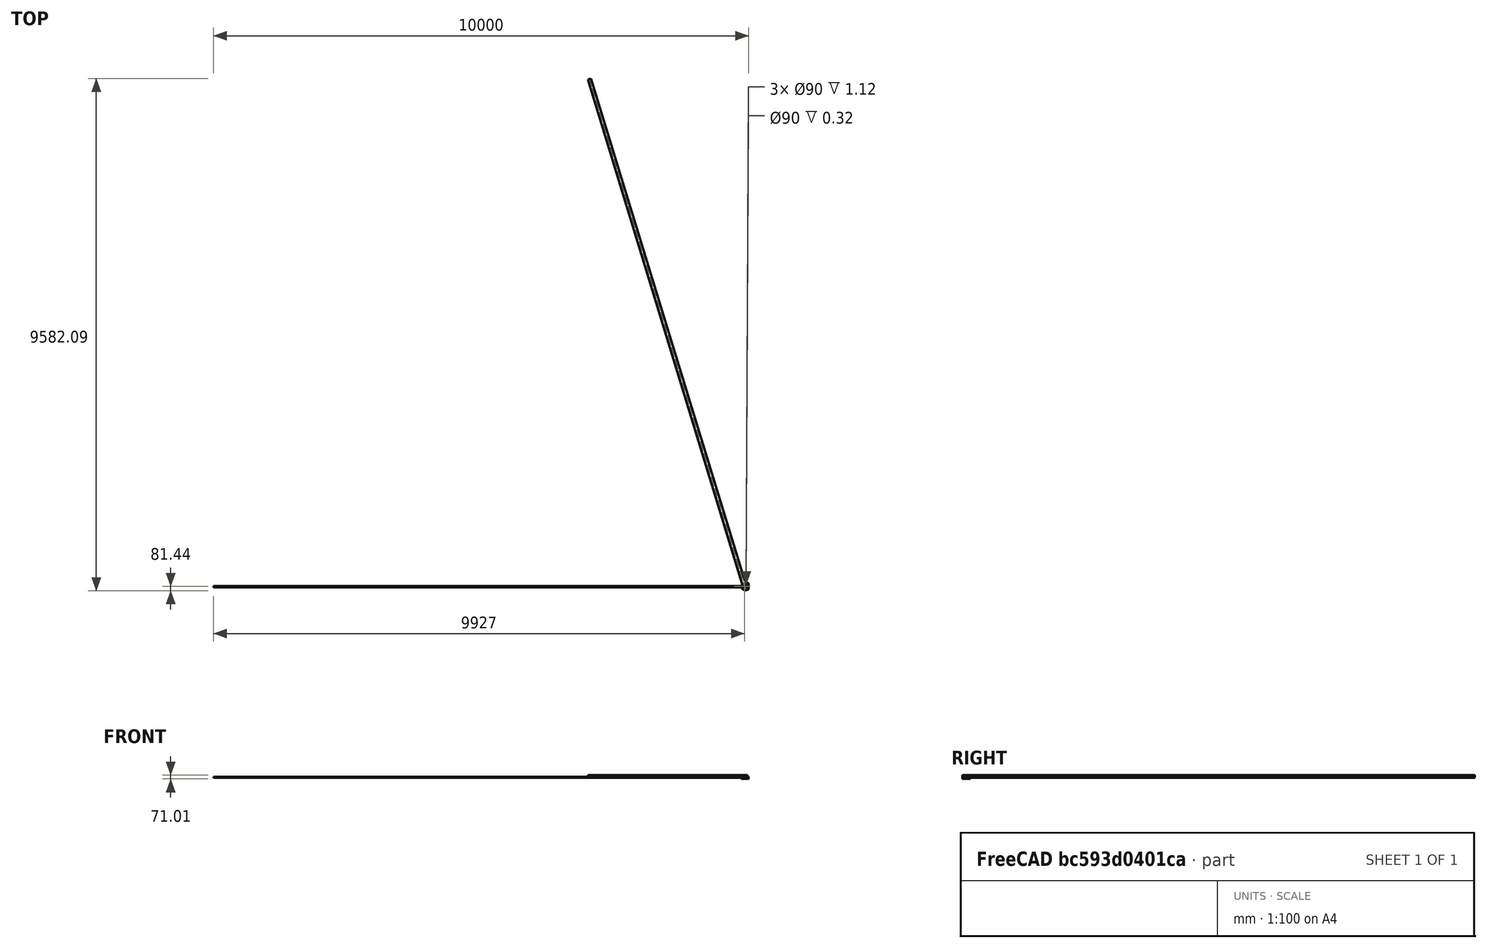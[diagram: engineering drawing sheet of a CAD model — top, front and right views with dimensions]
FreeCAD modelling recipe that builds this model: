
FCSTD DOCUMENT  (FreeCAD 0.16R)
Label: chainguard25TRev1.V2
License: All rights reserved
LicenseURL: http://en.wikipedia.org/wiki/All_rights_reserved
objects: Sketcher::SketchObject×14, PartDesign::Pocket×8, PartDesign::Pad×5, PartDesign::Fillet×5, Part::FeaturePython×3, Mesh::Feature×3
note: 48 computed .brp shape members not serialized (recipe doc carries the construction recipe); baked Part::Feature solids carry a one-line shape summary decoded from their .brp

FEATURE [Sketcher::SketchObject] Sketch001
  sketch-geometry (7):
    g0: LineSegment StartX=60 StartY=64 StartZ=0 EndX=0 EndY=64 EndZ=0
    g1: LineSegment StartX=60 StartY=-64 StartZ=0 EndX=0 EndY=-64 EndZ=0
    g2: ArcOfCircle CenterX=8.21903e-05 CenterY=0 CenterZ=0 NormalX=0 NormalY=0 NormalZ=1 Radius=64 StartAngle=1.5708 EndAngle=4.71239
    g3: Circle CenterX=0 CenterY=0 CenterZ=0 NormalX=0 NormalY=0 NormalZ=1 Radius=45
    g4: ArcOfCircle CenterX=60 CenterY=51 CenterZ=0 NormalX=0 NormalY=0 NormalZ=1 Radius=13 StartAngle=0 EndAngle=1.5708
    g5: ArcOfCircle CenterX=60 CenterY=-51 CenterZ=0 NormalX=0 NormalY=0 NormalZ=1 Radius=13 StartAngle=4.71239 EndAngle=6.28319
    g6: LineSegment StartX=73 StartY=51 StartZ=0 EndX=73 EndY=-51 EndZ=0
  constraints (23):
    c: Horizontal(g0)
    c: Horizontal(g1)
    c: Coincident(g2,g1)
    c: Coincident(g0,g2)
    c: DistanceX(g1,g0) = 0
    c: Equal(g0,g1)
    c: DistanceY(g1,g0) = 128
    c: Radius(g2) = 64
    c: Symmetric(g1,g0,g-1)
    c: Radius(g3) = 45
    c: Coincident(g3,g-1)
    c: PointOnObject(g4,g0)
    c: Radius(g4) = 13
    c: DistanceX(g0,g0) = 60
    c: Equal(g5,g4)
    c: Vertical(g6)
    c: DistanceX(g-1,g6) = 73
    c: Symmetric(g6,g6,g-1)
    c: DistanceY(g6,g6) = 102
    c: Coincident(g4,g6)
    c: Coincident(g5,g6)
    c: Coincident(g1,g5)
    c: Coincident(g0,g4)
FEATURE [PartDesign::Pad] Pad  label="Faceplate"
  Length = 1.12
  Length2 = 100
  Reversed = true
  Sketch = -> Sketch001
  Type = 0
FEATURE [Sketcher::SketchObject] Sketch002
  sketch-geometry (8):
    g0: LineSegment StartX=60 StartY=64 StartZ=0 EndX=0 EndY=64 EndZ=0
    g1: LineSegment StartX=60 StartY=-64 StartZ=0 EndX=0 EndY=-64 EndZ=0
    g2: ArcOfCircle CenterX=6.44712e-05 CenterY=0 CenterZ=0 NormalX=0 NormalY=0 NormalZ=1 Radius=64 StartAngle=1.5708 EndAngle=4.71239
    g3: LineSegment StartX=0 StartY=62 StartZ=0 EndX=60 EndY=62 EndZ=0
    g4: LineSegment StartX=0 StartY=-62 StartZ=0 EndX=60 EndY=-62 EndZ=0
    g5: LineSegment StartX=60 StartY=64 StartZ=0 EndX=60 EndY=62 EndZ=0
    g6: LineSegment StartX=60 StartY=-62 StartZ=0 EndX=60 EndY=-64 EndZ=0
    g7: ArcOfCircle CenterX=1.45954e-05 CenterY=0 CenterZ=0 NormalX=0 NormalY=0 NormalZ=1 Radius=62 StartAngle=1.5708 EndAngle=4.71239
  constraints (25):
    c: Horizontal(g0)
    c: Horizontal(g1)
    c: Coincident(g2,g1)
    c: Coincident(g0,g2)
    c: DistanceX(g1,g0) = 0
    c: Equal(g0,g1)
    c: DistanceY(g1,g0) = 128
    c: Radius(g2) = 64
    c: Symmetric(g1,g0,g-1)
    c: Radius(g7) = 62
    c: Parallel(g0,g3)
    c: DistanceY(g3,g0) = 2
    c: DistanceY(g1,g4) = 2
    c: Parallel(g4,g1)
    c: DistanceX(g0,g3) = 0
    c: DistanceX(g4) = 0
    c: DistanceX(g0) = 60
    c: Equal(g3,g0)
    c: Equal(g4,g0)
    c: Coincident(g4,g6)
    c: Coincident(g6,g1)
    c: Coincident(g5,g3)
    c: Coincident(g5,g0)
    c: Coincident(g7,g3)
    c: Coincident(g7,g4)
FEATURE [PartDesign::Pad] Pad001  label="Connector"
  Length = 8
  Length2 = 100
  Sketch = -> Sketch002
  Type = 0
FEATURE [Sketcher::SketchObject] Sketch004  label="BossST"
  sketch-geometry (4):
    g0: LineSegment StartX=42 StartY=-62 StartZ=0 EndX=2 EndY=-62 EndZ=0
    g1: LineSegment StartX=2 StartY=-62 StartZ=0 EndX=2 EndY=-78.2292 EndZ=0
    g2: LineSegment StartX=42 StartY=-66 StartZ=0 EndX=42 EndY=-62 EndZ=0
    g3: LineSegment StartX=2 StartY=-78.2292 StartZ=0 EndX=42 EndY=-66 EndZ=0
  constraints (12):
    c: Coincident(g0,g1)
    c: Vertical(g1)
    c: Vertical(g2)
    c: DistanceX(g0,g0) = 40
    c: DistanceX(g-1,g1) = 2
    c: Angle(g3) = 0.296706
    c: DistanceY(g0,g-1) = 62
    c: Horizontal(g0)
    c: DistanceY(g2,g2) = 4
    c: Coincident(g2,g0)
    c: Coincident(g3,g2)
    c: Coincident(g1,g3)
FEATURE [Sketcher::SketchObject] Sketch007
  Placement = pos=(0,0,45) rot=(0,0,1;0rad)
  sketch-geometry (4):
    g0: LineSegment StartX=-4.66376 StartY=-53.9534 StartZ=0 EndX=-5.90948 EndY=-71.4651 EndZ=0
    g1: LineSegment StartX=-5.90948 StartY=-71.4651 StartZ=0 EndX=38.1328 EndY=-58 EndZ=0
    g2: LineSegment StartX=38.1328 StartY=-58 StartZ=0 EndX=37.116 EndY=-54.0061 EndZ=0
    g3: LineSegment StartX=37.116 StartY=-54.0061 StartZ=0 EndX=-4.66376 EndY=-53.9534 EndZ=0
  constraints (9):
    c: Coincident(g0,g1)
    c: Coincident(g1,g2)
    c: Coincident(g2,g3)
    c: Coincident(g0,g3)
    c: Distance(g3) = 41.7798
    c: Distance(g0) = 17.5559
    c: Distance(g1) = 46.0546
    c: Distance(g2) = 4.12132
    c: DistanceX(g0,g-1) = 4.66376
FEATURE [PartDesign::Pocket] Pocket002  label="STpocket1"
  Length = 30
  Sketch = -> Sketch007
  Type = 0
FEATURE [Sketcher::SketchObject] Sketch
  Support = -> Pad [Face8]
  sketch-geometry (4):
    g0: LineSegment StartX=65 StartY=35 StartZ=0 EndX=73 EndY=35 EndZ=0
    g1: LineSegment StartX=73 StartY=35 StartZ=0 EndX=73 EndY=-35 EndZ=0
    g2: LineSegment StartX=73 StartY=-35 StartZ=0 EndX=65 EndY=-35 EndZ=0
    g3: LineSegment StartX=65 StartY=-35 StartZ=0 EndX=65 EndY=35 EndZ=0
  constraints (12):
    c: Coincident(g0,g1)
    c: Coincident(g1,g2)
    c: Coincident(g2,g3)
    c: Coincident(g3,g0)
    c: Horizontal(g0)
    c: Horizontal(g2)
    c: Vertical(g1)
    c: Vertical(g3)
    c: Symmetric(g0,g2,g-1)
    c: DistanceX(g0,g0) = 8
    c: DistanceX(g-1,g0) = 73
    c: DistanceY(g3,g3) = 70
FEATURE [PartDesign::Pad] Pad003  label="SyncStiffener"
  Length = 3
  Length2 = 100
  Sketch = -> Sketch
  Type = 0
FEATURE [Sketcher::SketchObject] Sketch008
  Placement = pos=(0,0,3) rot=(0,0,1;0rad)
  Support = -> Pad003 [Face14]
  sketch-geometry (4):
    g0: LineSegment StartX=67 StartY=8 StartZ=0 EndX=73 EndY=8 EndZ=0
    g1: LineSegment StartX=73 StartY=8 StartZ=0 EndX=73 EndY=-22 EndZ=0
    g2: LineSegment StartX=73 StartY=-22 StartZ=0 EndX=67 EndY=-22 EndZ=0
    g3: LineSegment StartX=67 StartY=-22 StartZ=0 EndX=67 EndY=8 EndZ=0
  constraints (12):
    c: Coincident(g0,g1)
    c: Coincident(g1,g2)
    c: Coincident(g2,g3)
    c: Coincident(g3,g0)
    c: Horizontal(g0)
    c: Horizontal(g2)
    c: Vertical(g1)
    c: Vertical(g3)
    c: DistanceX(g0) = 73
    c: DistanceX(g0,g0) = 6
    c: DistanceY(g1,g1) = 30
    c: DistanceY(g-1,g0) = 8
FEATURE [PartDesign::Pad] Pad004  label="SyncTubeBoss"
  Length = 41
  Length2 = 100
  Sketch = -> Sketch008
  Type = 0
FEATURE [Sketcher::SketchObject] Sketch009
  ExternalGeometry = -> [Pad004]
  Placement = pos=(73,0,0) rot=(0.57735,0.57735,0.57735;2.0944rad)
  Support = -> Pad004 [Face15]
  sketch-geometry (1):
    g0: Circle CenterX=-7 CenterY=30 CenterZ=0 NormalX=0 NormalY=0 NormalZ=1 Radius=11.2
  constraints (3):
    c: DistanceX(g0,g-3) = 15
    c: DistanceY(g-1,g0) = 30
    c: Radius(g0) = 11.2
FEATURE [PartDesign::Pocket] Pocket003  label="SyncTubeHole"
  Length = 5
  Sketch = -> Sketch009
  Type = 1
FEATURE [Sketcher::SketchObject] Sketch010
  Placement = pos=(73,0,0) rot=(0.57735,0.57735,0.57735;2.0944rad)
  Support = -> Pocket003 [Face15]
  sketch-geometry (5):
    g0: LineSegment StartX=-7 StartY=48 StartZ=0 EndX=15 EndY=36 EndZ=0
    g1: LineSegment StartX=15 StartY=36 StartZ=0 EndX=15 EndY=54.3744 EndZ=0
    g2: LineSegment StartX=15 StartY=54.3744 StartZ=0 EndX=-29 EndY=54.3744 EndZ=0
    g3: LineSegment StartX=-29 StartY=54.3744 StartZ=0 EndX=-29 EndY=36 EndZ=0
    g4: LineSegment StartX=-29 StartY=36 StartZ=0 EndX=-7 EndY=48 EndZ=0
  constraints (15):
    c: Coincident(g0,g1)
    c: Vertical(g1)
    c: Coincident(g1,g2)
    c: Horizontal(g2)
    c: Coincident(g2,g3)
    c: Coincident(g3,g4)
    c: Coincident(g0,g4)
    c: DistanceX(g0,g-1) = 7
    c: DistanceX(g3,g0) = 22
    c: DistanceX(g0,g0) = 22
    c: Vertical(g3)
    c: DistanceY(g0,g0) = 12
    c: DistanceY(g3,g0) = 12
    c: DistanceY(g-1,g0) = 48
    c: DistanceY(g1,g1) = 18.3744
FEATURE [PartDesign::Pocket] Pocket004  label="SyncTubeBevel"
  Length = 5
  Sketch = -> Sketch010
  Type = 1
FEATURE [PartDesign::Fillet] Fillet  label="Fillet_Face"
  Base = -> Pocket004 [Edge4,Edge12,Edge20,Edge21,Edge22,Edge6,Edge23]
  Radius = 0.8
FEATURE [Sketcher::SketchObject] Sketch011
  Placement = pos=(0,64,0) rot=(0,0.707107,0.707107;3.14159rad)
  Support = -> Pad001 [Face1]
  sketch-geometry (4):
    g0: LineSegment StartX=-53.9525 StartY=8.40024 StartZ=0 EndX=-64.2023 EndY=10.8364 EndZ=0
    g1: LineSegment StartX=-64.2023 StartY=10.8364 StartZ=0 EndX=-61.1872 EndY=0.741769 EndZ=0
    g2: LineSegment StartX=-61.1872 StartY=0.741769 StartZ=0 EndX=-53.9525 EndY=8.40024 EndZ=0
    g3: Circle [constr] CenterX=-59.7806 CenterY=6.65947 CenterZ=0 NormalX=0 NormalY=0 NormalZ=1 Radius=6.08256
  constraints (14):
    c: Coincident(g0,g1)
    c: Coincident(g1,g2)
    c: Coincident(g2,g0)
    c: Equal(g0,g1)
    c: Equal(g0,g2)
    c: PointOnObject(g0,g3)
    c: PointOnObject(g1,g3)
    c: PointOnObject(g2,g3)
    c: DistanceY(g-1,g0) = 8.40024
    c: DistanceX(g0,g-1) = 53.9525
    c: Equal(g2,g0)
    c: Equal(g0,g1)
    c: Distance(g2) = 10.5353
    c: Angle(g0) = 2.90824
FEATURE [PartDesign::Pocket] Pocket005  label="Bevel_connector"
  Length = 5
  Sketch = -> Sketch011
  Type = 1
FEATURE [PartDesign::Pad] Pad005  label="STBoss"
  Length = 45
  Length2 = 1
  Sketch = -> Sketch004
  Type = 4
FEATURE [Sketcher::SketchObject] Sketch012
  Placement = pos=(22.0436,-72.1013,0) rot=(0.978386,0.146221,0.146221;1.59265rad)
  Support = -> Pad005 [Face3]
  sketch-geometry (1):
    g0: Circle CenterX=0 CenterY=30 CenterZ=0 NormalX=0 NormalY=0 NormalZ=1 Radius=11.2
  constraints (3):
    c: DistanceY(g-1,g0) = 30
    c: Radius(g0) = 11.2
    c: DistanceX(g0,g-1) = 0
FEATURE [PartDesign::Pocket] Pocket006  label="STPocket1"
  Length = 5
  Sketch = -> Sketch012
  Type = 1
FEATURE [Sketcher::SketchObject] Sketch013
  Placement = pos=(22.0436,-72.1013,0) rot=(0.978386,0.146221,0.146221;1.59265rad)
  Support = -> Pocket006 [Face7]
  sketch-geometry (5):
    g0: LineSegment StartX=0 StartY=56.1345 StartZ=0 EndX=33.1882 EndY=29.2826 EndZ=0
    g1: LineSegment StartX=33.1882 StartY=29.2826 StartZ=0 EndX=33.1882 EndY=69.8913 EndZ=0
    g2: LineSegment StartX=33.1882 StartY=69.8913 StartZ=0 EndX=-31.957 EndY=69.8913 EndZ=0
    g3: LineSegment StartX=-31.957 StartY=69.8913 StartZ=0 EndX=-31.957 EndY=27.8285 EndZ=0
    g4: LineSegment StartX=-31.957 StartY=27.8285 StartZ=0 EndX=0 EndY=56.1345 EndZ=0
  constraints (16):
    c: Coincident(g0,g1)
    c: Coincident(g1,g2)
    c: Coincident(g2,g3)
    c: Vertical(g3)
    c: Coincident(g3,g4)
    c: Coincident(g4,g0)
    c: Vertical(g1)
    c: Horizontal(g2)
    c: Equal(g0,g4)
    c: DistanceX(g0,g-1) = 0
    c: DistanceX(g2,g2) = 65.1452
    c: DistanceY(g3,g3) = 42.0628
    c: Distance(g4) = 42.6905
    c: Equal(g0,g4)
    c: Angle(g0) = -0.680253
    c: DistanceY(g-1,g0) = 56.1345
FEATURE [PartDesign::Pocket] Pocket  label="STPocket2"
  Length = 5
  Sketch = -> Sketch013
  Type = 1
FEATURE [Sketcher::SketchObject] Sketch014
  ExternalGeometry = -> [Pocket]
  Placement = pos=(0,0,45) rot=(0,0,1;0rad)
  Support = -> Pocket [Face5]
  sketch-geometry (4):
    g0: LineSegment StartX=45.8904 StartY=-57.7868 StartZ=0 EndX=-5.58537 EndY=-74.5488 EndZ=0
    g1: LineSegment StartX=-5.58537 StartY=-74.5488 StartZ=0 EndX=-10.2638 EndY=-60.1813 EndZ=0
    g2: LineSegment StartX=-10.2638 StartY=-60.1813 StartZ=0 EndX=41.2119 EndY=-43.4193 EndZ=0
    g3: LineSegment StartX=41.2119 StartY=-43.4193 StartZ=0 EndX=45.8904 EndY=-57.7868 EndZ=0
  constraints (14):
    c: Coincident(g0,g1)
    c: Coincident(g1,g2)
    c: Coincident(g2,g3)
    c: Coincident(g0,g3)
    c: Equal(g3,g1)
    c: Parallel(g3,g1)
    c: Distance(g-3) = 26.3326
    c: Distance(g-3) = 26.3326
    c: Angle(g1,g2) = 1.5708
    c: Distance(g3) = 15.11
    c: Distance(g-3,g0) = 6
    c: DistanceY(g-3,g1) = 15.5953
    c: DistanceX(g1,g-3) = 20.286
    c: Distance(g2) = 54.1361
FEATURE [PartDesign::Pocket] Pocket007
  Length = 31
  Sketch = -> Sketch014
  Type = 0
FEATURE [PartDesign::Fillet] Fillet001
  Base = -> Pocket007 [Edge10,Edge7,Edge23,Edge24]
  Radius = 1
FEATURE [PartDesign::Fillet] Fillet002
  Base = -> Fillet001 [Edge21,Edge24,Edge25,Edge26,Edge6,Edge19,Edge20,Edge4,Edge13,Edge33,Edge27,Edge16,Edge9,Edge15,Edge17,Edge18,Edge3,Edge5,Edge23]
  Radius = 1
FEATURE [PartDesign::Fillet] Fillet003
  Base = -> Fillet [Edge55,Edge67,Edge63,Edge69,Edge64,Edge68,Edge54,Edge53,Edge65,Edge61]
  Radius = 1
FEATURE [Sketcher::SketchObject] Sketch015
  Placement = pos=(2,0,0) rot=(0.57735,-0.57735,-0.57735;2.0944rad)
  Support = -> Fillet002 [Face15]
FEATURE [Sketcher::SketchObject] Sketch016
  Placement = pos=(2,0,0) rot=(0.57735,-0.57735,-0.57735;2.0944rad)
  Support = -> Fillet002 [Face15]
  sketch-geometry (3):
    g0: LineSegment StartX=80 StartY=13 StartZ=0 EndX=70 EndY=-4.32051 EndZ=0
    g1: LineSegment StartX=70 StartY=-4.32051 StartZ=0 EndX=90 EndY=-4.32051 EndZ=0
    g2: LineSegment StartX=90 StartY=-4.32051 StartZ=0 EndX=80 EndY=13 EndZ=0
  constraints (10):
    c: Coincident(g0,g1)
    c: Horizontal(g1)
    c: Coincident(g1,g2)
    c: Coincident(g2,g0)
    c: Equal(g2,g0)
    c: Equal(g0,g1)
    c: Distance(g2) = 20
    c: Angle(g0) = -2.0944
    c: DistanceY(g-1,g0) = 13
    c: DistanceX(g-1,g0) = 80
FEATURE [PartDesign::Pocket] Pocket008
  Length = 5
  Sketch = -> Sketch016
  Type = 1
FEATURE [PartDesign::Fillet] Fillet004
  Base = -> Pocket008 [Edge49,Edge50,Edge12,Edge47,Edge51]
  Radius = 1
FEATURE [Part::FeaturePython] refine  label="refine_Fillet003"  # WARN: FeaturePython — macro-defined, semantics opaque (R4)
  Base = -> Fillet003
FEATURE [Part::FeaturePython] refine001  label="refine_Fillet004"  # WARN: FeaturePython — macro-defined, semantics opaque (R4)
  Base = -> Fillet004
FEATURE [Part::FeaturePython] refine002  label="refine_Bevel_connector"  # WARN: FeaturePython — macro-defined, semantics opaque (R4)
  Base = -> Pocket005
FEATURE [Mesh::Feature] Mesh  label="refine_Fillet003 (Meshed)"
FEATURE [Mesh::Feature] Mesh001  label="refine_Fillet004 (Meshed)"
FEATURE [Mesh::Feature] Mesh002  label="refine_Bevel_connector (Meshed)"
